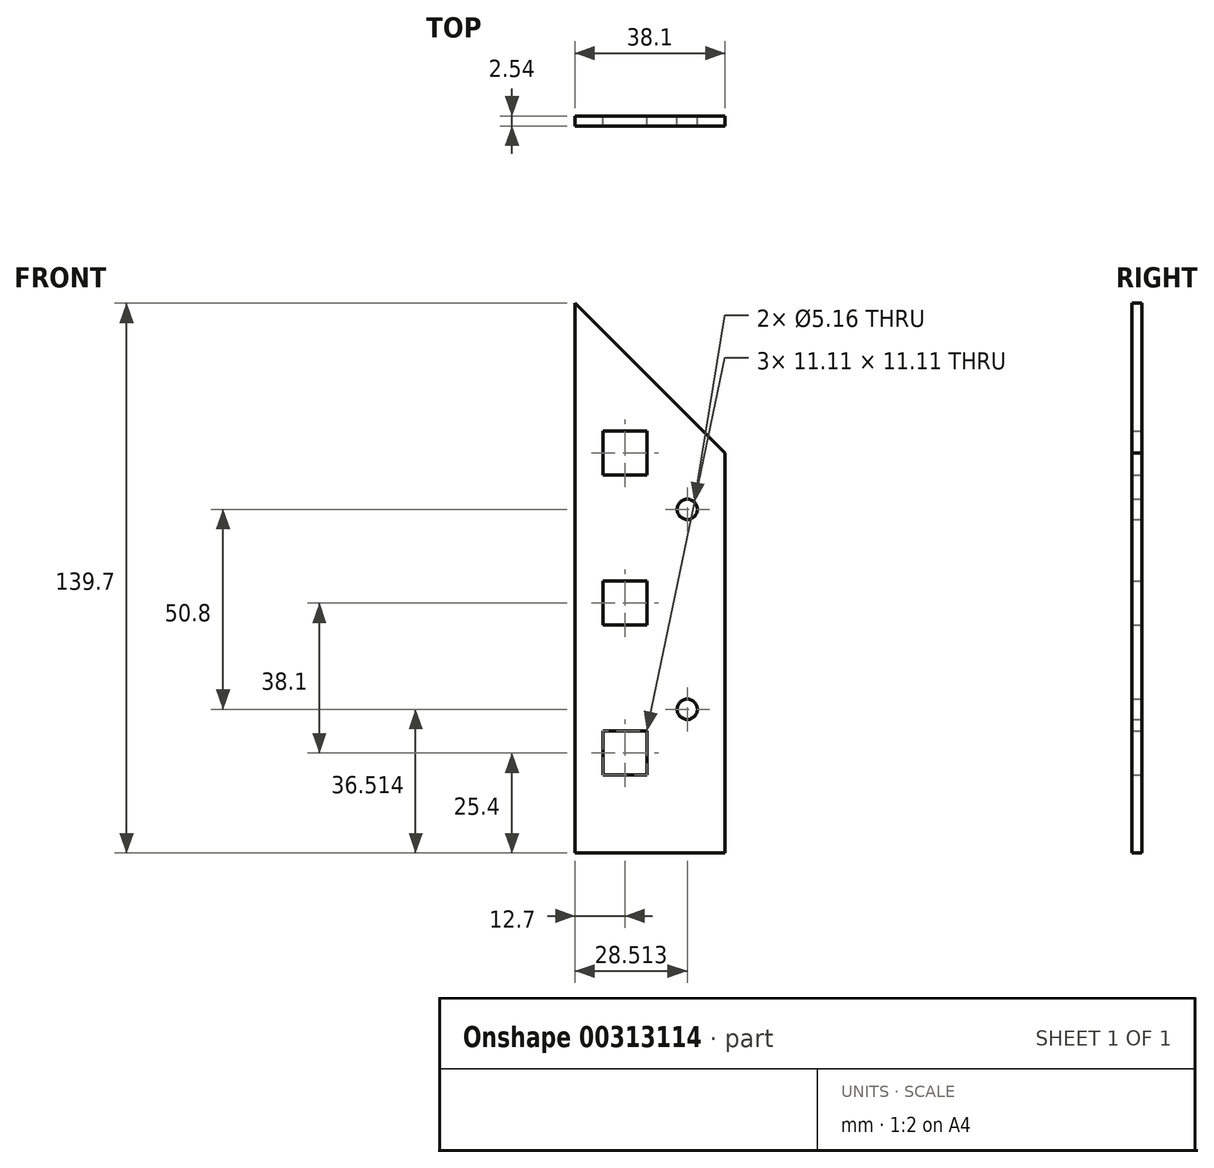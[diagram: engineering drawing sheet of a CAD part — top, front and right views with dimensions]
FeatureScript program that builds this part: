
annotation { "Feature Type Name" : "Feature", "Feature Type Description" : "" }
export const myFeature = defineFeature(function(context is Context, id is Id, definition is map)
    precondition{}
    {
        {
            var Q0;
            Q0=qCreatedBy(makeId("Front.planeOp"),FACE);
            var sketch = newSketch(context, id + "F0", { "sketchPlane" : qUnion([Q0])});
            skLineSegment(sketch, "E0.bottom", {"start": v(0, 0) * mm, "end": v(38.1, 0) * mm});
            skLineSegment(sketch, "E0.left", {"start": v(0, 0) * mm, "end": v(0, 139.7) * mm});
            skLineSegment(sketch, "E0.right", {"start": v(38.1, 0) * mm, "end": v(38.1, 101.6) * mm});
            skCircle(sketch, "E1", {"center": v(28.51, 87.31) * mm, "radius": 2.58 * mm});
            skCircle(sketch, "E2", {"center": v(28.51, 36.51) * mm, "radius": 2.58 * mm});
            skLineSegment(sketch, "E3.bottom", {"start": v(18.26, 96.04) * mm, "end": v(7.14, 96.04) * mm});
            skLineSegment(sketch, "E3.top", {"start": v(18.26, 107.16) * mm, "end": v(7.14, 107.16) * mm});
            skLineSegment(sketch, "E3.left", {"start": v(18.26, 96.04) * mm, "end": v(18.26, 107.16) * mm});
            skLineSegment(sketch, "E3.right", {"start": v(7.14, 96.04) * mm, "end": v(7.14, 107.16) * mm});
            skPoint(sketch, "E3.middle", {"position": v(12.7, 101.6) * mm});
            skLineSegment(sketch, "E4.bottom", {"start": v(18.26, 57.94) * mm, "end": v(7.14, 57.94) * mm});
            skLineSegment(sketch, "E4.top", {"start": v(18.26, 69.06) * mm, "end": v(7.14, 69.06) * mm});
            skLineSegment(sketch, "E4.left", {"start": v(18.26, 57.94) * mm, "end": v(18.26, 69.06) * mm});
            skLineSegment(sketch, "E4.right", {"start": v(7.14, 57.94) * mm, "end": v(7.14, 69.06) * mm});
            skPoint(sketch, "E4.middle", {"position": v(12.7, 63.5) * mm});
            skPoint(sketch, "E4.middle.positionSnap0", {"position": v(12.7, 96.04) * mm});
            skPoint(sketch, "E4.centerSnap0", {"position": v(12.7, 96.04) * mm});
            skLineSegment(sketch, "E5.bottom", {"start": v(18.26, 30.96) * mm, "end": v(7.14, 30.96) * mm});
            skLineSegment(sketch, "E5.top", {"start": v(18.26, 19.84) * mm, "end": v(7.14, 19.84) * mm});
            skLineSegment(sketch, "E5.left", {"start": v(18.26, 30.96) * mm, "end": v(18.26, 19.84) * mm});
            skLineSegment(sketch, "E5.right", {"start": v(7.14, 30.96) * mm, "end": v(7.14, 19.84) * mm});
            skPoint(sketch, "E5.middle", {"position": v(12.7, 25.4) * mm});
            skLineSegment(sketch, "E6", {"start": v(0, 139.7) * mm, "end": v(38.1, 101.6) * mm});
            skSolve(sketch);
        }
        {
            var Q0;
            Q0 = qSketchRegion(id + "F0", true);
            extrude(context, id + "F1", {"entities" : qUnion([Q0]), "endBound" : BoundingType.SYMMETRIC, "depth" : 2.54 * mm});
        }
    });
